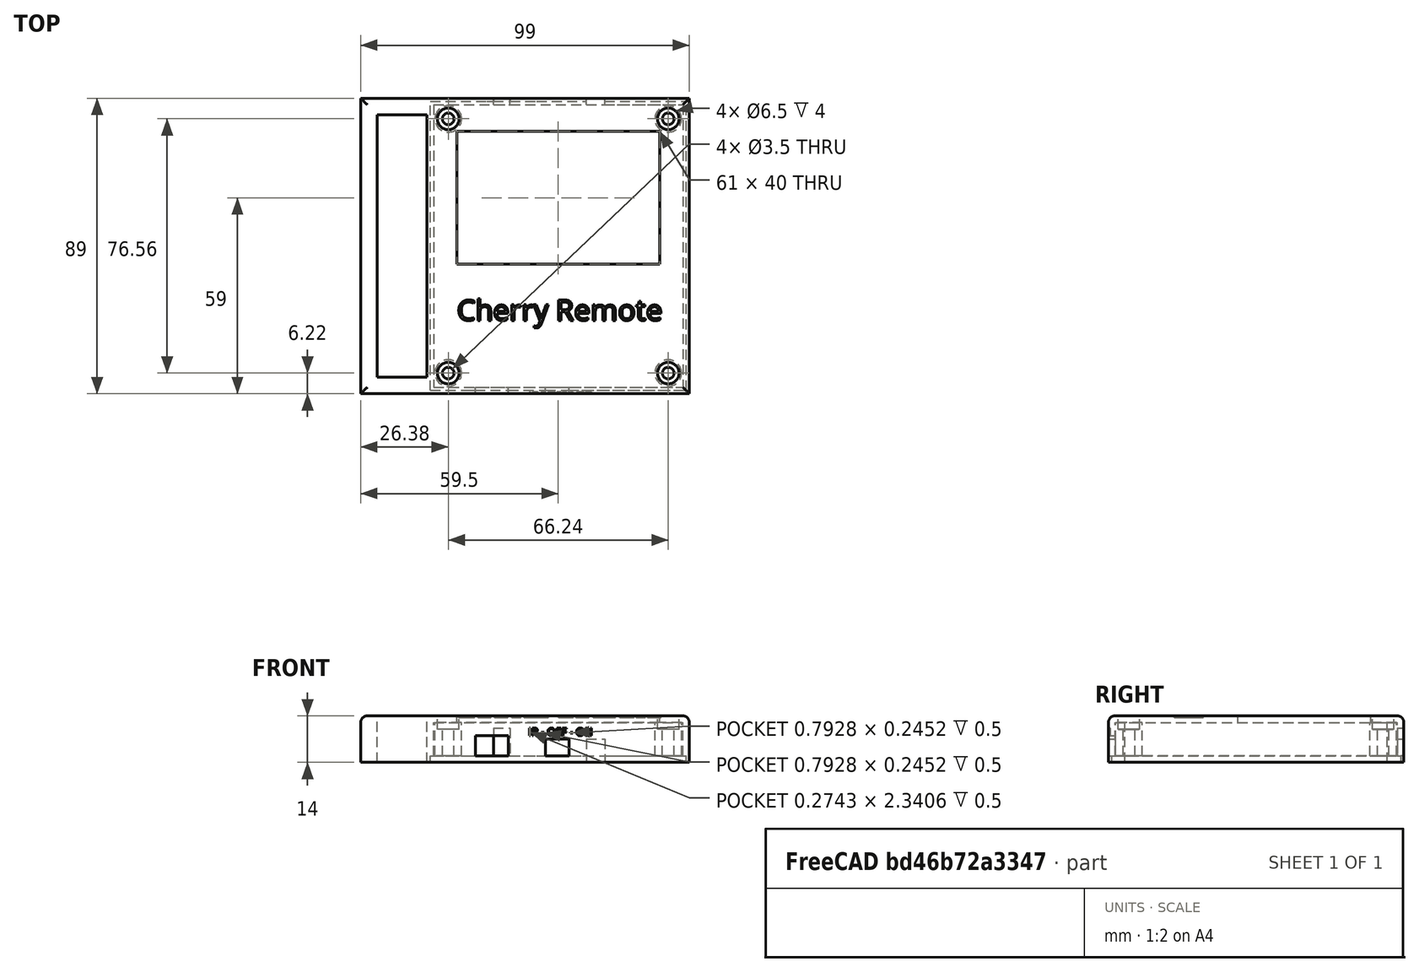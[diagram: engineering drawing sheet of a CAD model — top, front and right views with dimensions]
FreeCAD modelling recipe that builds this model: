
FCSTD DOCUMENT  (FreeCAD 0.18R16131 (Git))
Label: remote_case_top
License: All rights reserved
LicenseURL: http://en.wikipedia.org/wiki/All_rights_reserved
objects: Part::Cut×18, Part::Box×14, Part::Cylinder×12, Part::MultiFuse×9, Part::Fillet×2, Part::Part2DObjectPython×2, Part::Extrusion×2
note: 59 computed .brp shape members not serialized (recipe doc carries the construction recipe); baked Part::Feature solids carry a one-line shape summary decoded from their .brp

FEATURE [Part::Box] Box  label="Cube"
  AttacherType = Attacher::AttachEngine3D
  Height = 14
  Length = 79
  Placement = pos=(-2,-2,0) rot=(0,0,1;0rad)
  Width = 89
FEATURE [Part::Box] Box001  label="Cube001"
  AttacherType = Attacher::AttachEngine3D
  Height = 12
  Length = 75
  Width = 85
FEATURE [Part::Box] Box003  label="Cube003"
  AttacherType = Attacher::AttachEngine3D
  Height = 2
  Length = 77
  Placement = pos=(-1,-1,0) rot=(0,0,1;0rad)
  Width = 87
FEATURE [Part::Cut] Cut
  Base = -> Box
  Tool = -> Box001
FEATURE [Part::Cut] Cut001
  Base = -> Cut
  Tool = -> Box003
FEATURE [Part::Cylinder] Cylinder
  Angle = 360
  AttacherType = Attacher::AttachEngine3D
  Height = 20
  Placement = pos=(4.38,4.22,0) rot=(0,0,1;0rad)
  Radius = 1.75
FEATURE [Part::Cylinder] Cylinder001
  Angle = 360
  AttacherType = Attacher::AttachEngine3D
  Height = 10
  Placement = pos=(70.62,4.22,0) rot=(0,0,1;0rad)
  Radius = 1.75
FEATURE [Part::Cylinder] Cylinder002
  Angle = 360
  AttacherType = Attacher::AttachEngine3D
  Height = 10
  Placement = pos=(70.62,80.78,0) rot=(0,0,1;0rad)
  Radius = 1.75
FEATURE [Part::Cylinder] Cylinder003
  Angle = 360
  AttacherType = Attacher::AttachEngine3D
  Height = 10
  Placement = pos=(4.38,80.78,0) rot=(0,0,1;0rad)
  Radius = 1.75
FEATURE [Part::Cylinder] Cylinder004
  Angle = 360
  AttacherType = Attacher::AttachEngine3D
  Height = 4
  Placement = pos=(4.38,4.22,10) rot=(0,0,1;0rad)
  Radius = 3.25
FEATURE [Part::Cylinder] Cylinder005
  Angle = 360
  AttacherType = Attacher::AttachEngine3D
  Height = 10
  Placement = pos=(4.38,4.22,2) rot=(0,0,1;0rad)
  Radius = 4
FEATURE [Part::MultiFuse] Fusion
  Shapes = -> [Cut001,Cylinder005]
FEATURE [Part::Cylinder] Cylinder006
  Angle = 360
  AttacherType = Attacher::AttachEngine3D
  Height = 10
  Placement = pos=(70.62,4.22,2) rot=(0,0,1;0rad)
  Radius = 4
FEATURE [Part::Cylinder] Cylinder007
  Angle = 360
  AttacherType = Attacher::AttachEngine3D
  Height = 4
  Placement = pos=(70.62,4.22,10) rot=(0,0,1;0rad)
  Radius = 3.25
FEATURE [Part::Cylinder] Cylinder008
  Angle = 360
  AttacherType = Attacher::AttachEngine3D
  Height = 10
  Placement = pos=(4.38,80.76,2) rot=(0,0,1;0rad)
  Radius = 4
FEATURE [Part::Cylinder] Cylinder009
  Angle = 360
  AttacherType = Attacher::AttachEngine3D
  Height = 10
  Placement = pos=(70.62,80.76,2) rot=(0,0,1;0rad)
  Radius = 4
FEATURE [Part::MultiFuse] Fusion001
  Shapes = -> [Fusion,Cylinder009]
FEATURE [Part::MultiFuse] Fusion002
  Shapes = -> [Fusion001,Cylinder008]
FEATURE [Part::MultiFuse] Fusion003
  Shapes = -> [Fusion002,Cylinder006]
FEATURE [Part::Cylinder] Cylinder010
  Angle = 360
  AttacherType = Attacher::AttachEngine3D
  Height = 4
  Placement = pos=(4.38,80.78,10) rot=(0,0,1;0rad)
  Radius = 3.25
FEATURE [Part::Cylinder] Cylinder011
  Angle = 360
  AttacherType = Attacher::AttachEngine3D
  Height = 4
  Placement = pos=(70.62,80.78,10) rot=(0,0,1;0rad)
  Radius = 3.25
FEATURE [Part::Cut] Cut002
  Base = -> Fusion003
  Tool = -> Cylinder010
FEATURE [Part::Cut] Cut003
  Base = -> Cut002
  Tool = -> Cylinder011
FEATURE [Part::Cut] Cut004
  Base = -> Cut003
  Tool = -> Cylinder007
FEATURE [Part::Cut] Cut005
  Base = -> Cut004
  Tool = -> Cylinder004
FEATURE [Part::Cut] Cut006
  Base = -> Cut005
  Tool = -> Cylinder
FEATURE [Part::Cut] Cut007
  Base = -> Cut006
  Tool = -> Cylinder001
FEATURE [Part::Cut] Cut008
  Base = -> Cut007
  Tool = -> Cylinder003
FEATURE [Part::Cut] Cut009
  Base = -> Cut008
  Tool = -> Cylinder002
FEATURE [Part::Box] Box004  label="Cube004"
  AttacherType = Attacher::AttachEngine3D
  Height = 8
  Length = 10
  Placement = pos=(12.5,-3,0) rot=(0,0,1;0rad)
  Width = 10
FEATURE [Part::Box] Box006  label="Cube006"
  AttacherType = Attacher::AttachEngine3D
  Height = 10.3
  Length = 5
  Placement = pos=(18,80,0) rot=(0,0,1;0rad)
  Width = 10
FEATURE [Part::Box] Box007  label="Cube007"
  AttacherType = Attacher::AttachEngine3D
  Height = 7
  Length = 5.5
  Placement = pos=(46,80,0) rot=(0,0,1;0rad)
  Width = 10
FEATURE [Part::Box] Box008  label="Cube008"
  AttacherType = Attacher::AttachEngine3D
  Height = 10
  Length = 61
  Placement = pos=(7,37,10) rot=(0,0,1;0rad)
  Width = 40
FEATURE [Part::Cut] Cut010
  Base = -> Cut009
  Tool = -> Box008
FEATURE [Part::Cut] Cut011
  Base = -> Cut010
  Tool = -> Box007
FEATURE [Part::Cut] Cut012
  Base = -> Cut011
  Tool = -> Box006
FEATURE [Part::Box] Box009  label="Cube009"
  AttacherType = Attacher::AttachEngine3D
  Height = 2
  Length = 30
  Placement = pos=(10,-2,0) rot=(0,0,1;0rad)
  Width = 1
FEATURE [Part::Box] Box010  label="Cube010"
  AttacherType = Attacher::AttachEngine3D
  Height = 2
  Length = 15
  Placement = pos=(16,86,0) rot=(0,0,1;0rad)
  Width = 1
FEATURE [Part::Box] Box011  label="Cube011"
  AttacherType = Attacher::AttachEngine3D
  Height = 14
  Length = 5
  Placement = pos=(-22,-2,0) rot=(0,0,1;0rad)
  Width = 89
FEATURE [Part::Box] Box012  label="Cube012"
  AttacherType = Attacher::AttachEngine3D
  Height = 14
  Length = 15
  Placement = pos=(-17,-2,0) rot=(0,0,1;0rad)
  Width = 5
FEATURE [Part::Box] Box013  label="Cube013"
  AttacherType = Attacher::AttachEngine3D
  Height = 14
  Length = 15
  Placement = pos=(-17,82,0) rot=(0,0,1;0rad)
  Width = 5
FEATURE [Part::MultiFuse] Fusion006
  Shapes = -> [Box011,Box012,Box013]
FEATURE [Part::Box] Box005  label="Cube005"
  AttacherType = Attacher::AttachEngine3D
  Height = 6
  Length = 6
  Placement = pos=(33.7,-2,0) rot=(0,0,1;0rad)
  Width = 5
FEATURE [Part::Cut] Cut013
  Base = -> Cut012
  Tool = -> Box005
FEATURE [Part::Cut] Cut014
  Base = -> Cut013
  Tool = -> Box004
FEATURE [Part::MultiFuse] Fusion004
  Shapes = -> [Box009,Cut014]
FEATURE [Part::MultiFuse] Fusion005
  Shapes = -> [Fusion004,Box010]
FEATURE [Part::Box] Box014  label="Cube014"
  AttacherType = Attacher::AttachEngine3D
  Height = 5
  Length = 7
  Placement = pos=(33.7,-3,2) rot=(0,0,1;0rad)
  Width = 10
FEATURE [Part::Fillet] Fillet001
  Base = -> Fusion005
  Edges = 3 edges r=2: [Edge34,Edge69,Edge97]
FEATURE [Part::MultiFuse] Fusion007
  Shapes = -> [Fillet001]
FEATURE [Part::Cut] Cut015
  Base = -> Fusion007
  Tool = -> Box014
FEATURE [Part::Fillet] Fillet
  Base = -> Fusion006
  Edges = 3 edges r=2: [Edge2,Edge19,Edge24]
FEATURE [Part::MultiFuse] Fusion008
  Shapes = -> [Cut015,Fillet]
FEATURE [Part::Part2DObjectPython] ShapeString  # Draft 2D object (typed FeaturePython)
  FontFile = <userpath>/A6E4-ED97/3dprinting/fonts/open-sans/OpenSans-Regular.ttf
  Placement = pos=(7,20,14) rot=(0,1,0;0rad)
  Size = 8
  String = Cherry Remote
  Tracking = 0
FEATURE [Part::Part2DObjectPython] ShapeString001  # Draft 2D object (typed FeaturePython)
  FontFile = <userpath>/A6E4-ED97/3dprinting/fonts/open-sans/OpenSans-Regular.ttf
  Placement = pos=(28.5,-9,8) rot=(1,0,0;1.5708rad)
  Size = 3
  String = IR - OFF - ON
  Tracking = 0
FEATURE [Part::Extrusion] Extrude
  Base = -> ShapeString
  Dir = (0,0,1)
  DirMode = 2
  FaceMakerClass = Part::FaceMakerBullseye
  LengthFwd = 0.5
  LengthRev = 0
  Placement = pos=(0,0,-0.5) rot=(0,0,1;0rad)
  Solid = false
  Symmetric = false
FEATURE [Part::Extrusion] Extrude001
  Base = -> ShapeString001
  Dir = (0,-1,2e-16)
  DirMode = 2
  FaceMakerClass = Part::FaceMakerBullseye
  LengthFwd = 0.5
  LengthRev = 0
  Placement = pos=(0,7.5,0) rot=(0,0,1;0rad)
  Solid = false
  Symmetric = false
FEATURE [Part::Cut] Cut016
  Base = -> Fusion008
  Tool = -> Extrude001
FEATURE [Part::Cut] Cut017
  Base = -> Cut016
  Tool = -> Extrude
